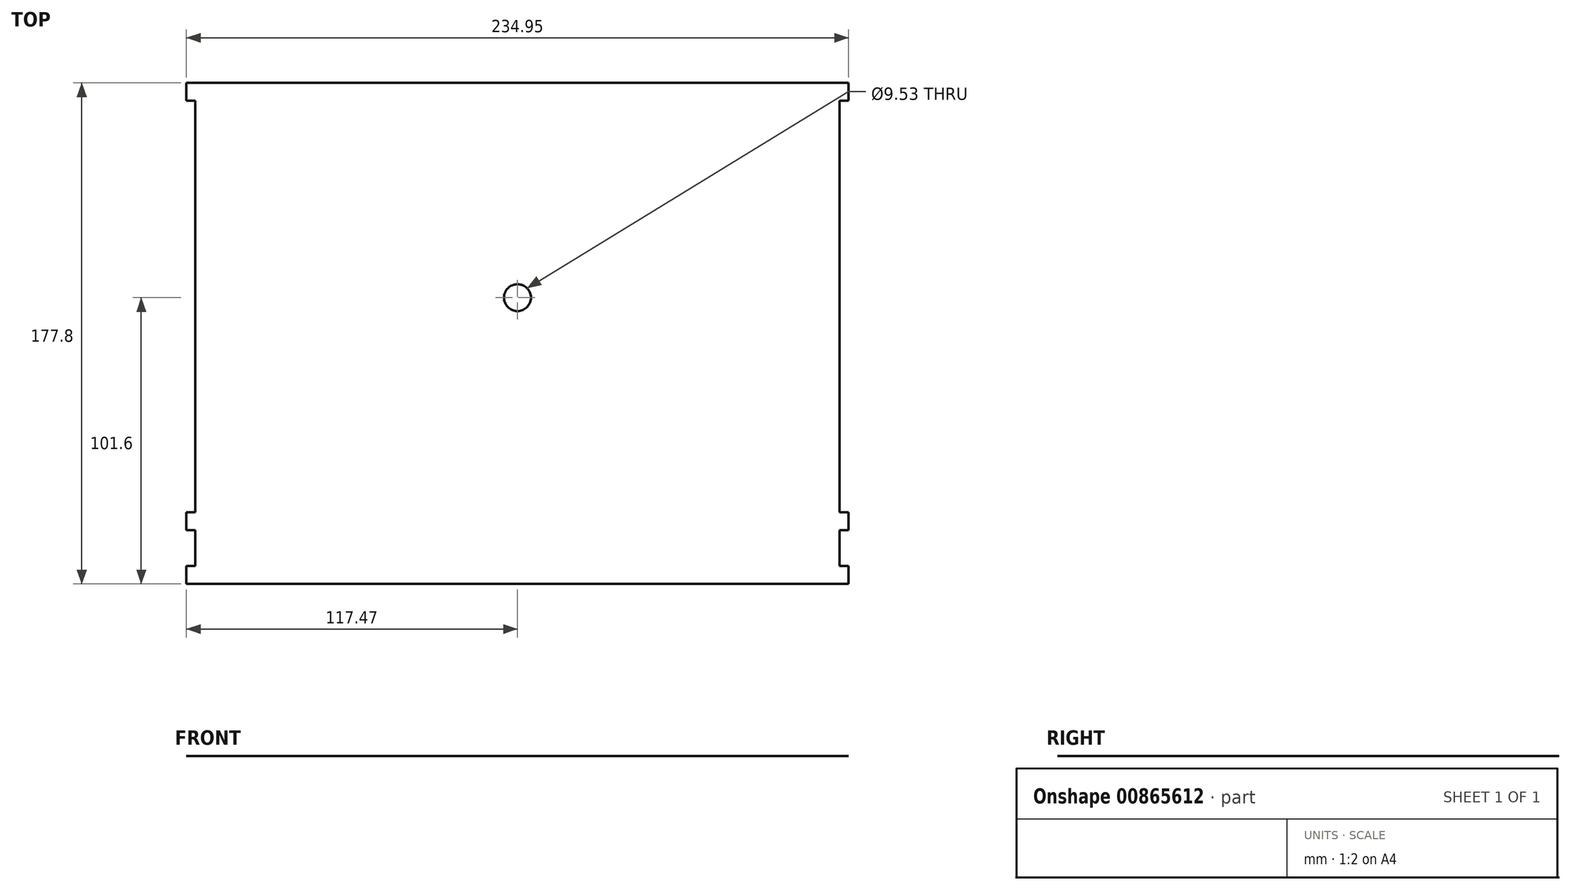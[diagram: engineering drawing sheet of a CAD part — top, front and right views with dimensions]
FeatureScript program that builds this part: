
annotation { "Feature Type Name" : "Feature", "Feature Type Description" : "" }
export const myFeature = defineFeature(function(context is Context, id is Id, definition is map)
    precondition{}
    {
        {
            var Q0;
            Q0=qCreatedBy(makeId("Top.planeOp"),FACE);
            var sketch = newSketch(context, id + "F0", { "sketchPlane" : qUnion([Q0])});
            skLineSegment(sketch, "E0.bottom", {"start": v(0, 0) * mm, "end": v(228.6, 0) * mm});
            skLineSegment(sketch, "E0.top", {"start": v(0, -177.8) * mm, "end": v(228.6, -177.8) * mm});
            skLineSegment(sketch, "E0.left", {"start": v(0, 0) * mm, "end": v(0, -177.8) * mm});
            skLineSegment(sketch, "E0.right", {"start": v(228.6, 0) * mm, "end": v(228.6, -177.8) * mm});
            skLineSegment(sketch, "E1.bottom", {"start": v(228.6, -177.8) * mm, "end": v(231.78, -177.8) * mm});
            skLineSegment(sketch, "E1.top", {"start": v(228.6, -171.45) * mm, "end": v(231.78, -171.45) * mm});
            skLineSegment(sketch, "E1.left", {"start": v(228.6, -177.8) * mm, "end": v(228.6, -171.45) * mm});
            skLineSegment(sketch, "E1.right", {"start": v(231.78, -177.8) * mm, "end": v(231.78, -171.45) * mm});
            skLineSegment(sketch, "E2.bottom", {"start": v(228.6, -158.75) * mm, "end": v(231.78, -158.75) * mm});
            skLineSegment(sketch, "E2.top", {"start": v(228.6, -152.4) * mm, "end": v(231.78, -152.4) * mm});
            skLineSegment(sketch, "E2.left", {"start": v(228.6, -158.75) * mm, "end": v(228.6, -152.4) * mm});
            skLineSegment(sketch, "E2.right", {"start": v(231.78, -158.75) * mm, "end": v(231.78, -152.4) * mm});
            skLineSegment(sketch, "E3.bottom", {"start": v(0, -177.8) * mm, "end": v(-3.17, -177.8) * mm});
            skLineSegment(sketch, "E3.top", {"start": v(0, -171.45) * mm, "end": v(-3.17, -171.45) * mm});
            skLineSegment(sketch, "E3.left", {"start": v(0, -177.8) * mm, "end": v(0, -171.45) * mm});
            skLineSegment(sketch, "E3.right", {"start": v(-3.17, -177.8) * mm, "end": v(-3.17, -171.45) * mm});
            skLineSegment(sketch, "E4.bottom", {"start": v(0, -158.75) * mm, "end": v(-3.17, -158.75) * mm});
            skLineSegment(sketch, "E4.top", {"start": v(0, -152.4) * mm, "end": v(-3.17, -152.4) * mm});
            skLineSegment(sketch, "E4.left", {"start": v(0, -158.75) * mm, "end": v(0, -152.4) * mm});
            skLineSegment(sketch, "E4.right", {"start": v(-3.17, -158.75) * mm, "end": v(-3.17, -152.4) * mm});
            skLineSegment(sketch, "E5.bottom", {"start": v(228.6, 0) * mm, "end": v(231.78, 0) * mm});
            skLineSegment(sketch, "E5.top", {"start": v(228.6, -6.35) * mm, "end": v(231.78, -6.35) * mm});
            skLineSegment(sketch, "E5.left", {"start": v(228.6, 0) * mm, "end": v(228.6, -6.35) * mm});
            skLineSegment(sketch, "E5.right", {"start": v(231.78, 0) * mm, "end": v(231.78, -6.35) * mm});
            skLineSegment(sketch, "E6.bottom", {"start": v(0, 0) * mm, "end": v(-3.18, 0) * mm});
            skLineSegment(sketch, "E6.top", {"start": v(0, -6.35) * mm, "end": v(-3.17, -6.35) * mm});
            skLineSegment(sketch, "E6.left", {"start": v(0, 0) * mm, "end": v(0, -6.35) * mm});
            skLineSegment(sketch, "E6.right", {"start": v(-3.18, 0) * mm, "end": v(-3.17, -6.35) * mm});
            skLineSegment(sketch, "E7", {"start": v(114.3, 0) * mm, "end": v(114.3, -177.8) * mm, "construction": true});
            skLineSegment(sketch, "E8", {"start": v(0, -76.2) * mm, "end": v(228.6, -76.2) * mm, "construction": true});
            skCircle(sketch, "E9", {"center": v(114.3, -76.2) * mm, "radius": 4.76 * mm});
            skSolve(sketch);
        }
        {
            var Q0;
            Q0=makeQuery(id+"F0.imprint","IMPRINT",FACE,{"disambiguationData":[TD([[makeQuery(id+"F0.imprint","IMPRINT",EDGE,{"derivedFrom":sQuery(id+"F0.wireOp",EDGE,"E0.bottom")}),-1.0]])]});
            var Q1;
            Q1=makeQuery(id+"F0.imprint","IMPRINT",FACE,{"disambiguationData":[TD([[makeQuery(id+"F0.imprint","IMPRINT",EDGE,{"derivedFrom":sQuery(id+"F0.wireOp",EDGE,"E4.bottom")}),-1.0]])]});
            var Q2;
            Q2=makeQuery(id+"F0.imprint","IMPRINT",FACE,{"disambiguationData":[TD([[makeQuery(id+"F0.imprint","IMPRINT",EDGE,{"derivedFrom":sQuery(id+"F0.wireOp",EDGE,"E3.bottom")}),-1.0]])]});
            var Q3;
            Q3=makeQuery(id+"F0.imprint","IMPRINT",FACE,{"disambiguationData":[TD([[makeQuery(id+"F0.imprint","IMPRINT",EDGE,{"derivedFrom":sQuery(id+"F0.wireOp",EDGE,"E6.bottom")}),1.0]])]});
            var Q4;
            Q4=makeQuery(id+"F0.imprint","IMPRINT",FACE,{"disambiguationData":[TD([[makeQuery(id+"F0.imprint","IMPRINT",EDGE,{"derivedFrom":sQuery(id+"F0.wireOp",EDGE,"E5.bottom")}),-1.0]])]});
            var Q5;
            Q5=makeQuery(id+"F0.imprint","IMPRINT",FACE,{"disambiguationData":[TD([[makeQuery(id+"F0.imprint","IMPRINT",EDGE,{"derivedFrom":sQuery(id+"F0.wireOp",EDGE,"E2.bottom")}),1.0]])]});
            var Q6;
            Q6=makeQuery(id+"F0.imprint","IMPRINT",FACE,{"disambiguationData":[TD([[makeQuery(id+"F0.imprint","IMPRINT",EDGE,{"derivedFrom":sQuery(id+"F0.wireOp",EDGE,"E1.bottom")}),1.0]])]});
            extrude(context, id + "F1", {"entities" : qUnion([Q0, Q1, Q2, Q3, Q4, Q5, Q6]), "depth" : 1 / 203.2 * mm, "offsetDistance" : 25.4 * mm});
        }
    });
